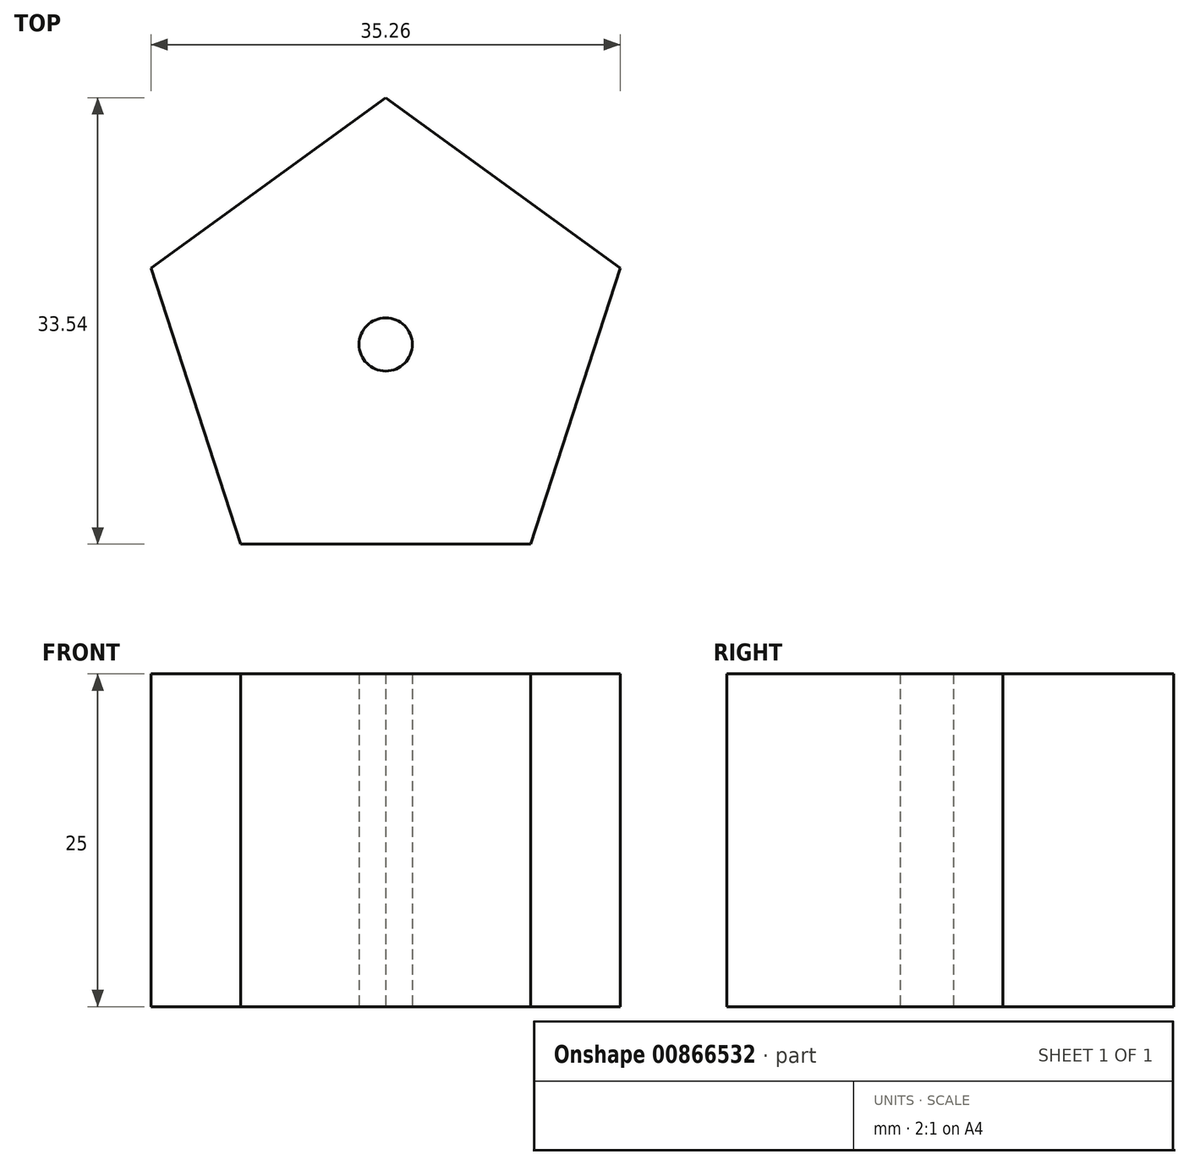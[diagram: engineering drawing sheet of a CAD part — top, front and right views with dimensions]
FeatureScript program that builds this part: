
annotation { "Feature Type Name" : "Feature", "Feature Type Description" : "" }
export const myFeature = defineFeature(function(context is Context, id is Id, definition is map)
    precondition{}
    {
        {
            var Q0;
            Q0=qCreatedBy(makeId("Top.planeOp"),FACE);
            var sketch = newSketch(context, id + "F0", { "sketchPlane" : qUnion([Q0])});
            skCircle(sketch, "E0.cCircle", {"center": v(0, 0) * mm, "radius": 15 * mm, "construction": true});
            skLineSegment(sketch, "E0.0", {"start": v(-17.63, 5.73) * mm, "end": v(0, 18.54) * mm});
            skLineSegment(sketch, "E0.1", {"start": v(0, 18.54) * mm, "end": v(17.63, 5.73) * mm});
            skLineSegment(sketch, "E0.2", {"start": v(17.63, 5.73) * mm, "end": v(10.9, -15) * mm});
            skLineSegment(sketch, "E0.3", {"start": v(10.9, -15) * mm, "end": v(-10.9, -15) * mm});
            skLineSegment(sketch, "E0.4", {"start": v(-10.9, -15) * mm, "end": v(-17.63, 5.73) * mm});
            skPoint(sketch, "E0.0.midPoint", {"position": v(-8.82, 12.14) * mm});
            skCircle(sketch, "E1", {"center": v(0, 0) * mm, "radius": 2 * mm});
            skSolve(sketch);
        }
        {
            var Q0;
            Q0 = qSketchRegion(id + "F0", true);
            extrude(context, id + "F1", {"entities" : qUnion([Q0]), "depth" : 25 * mm, "offsetDistance" : 25 * mm});
        }
    });
